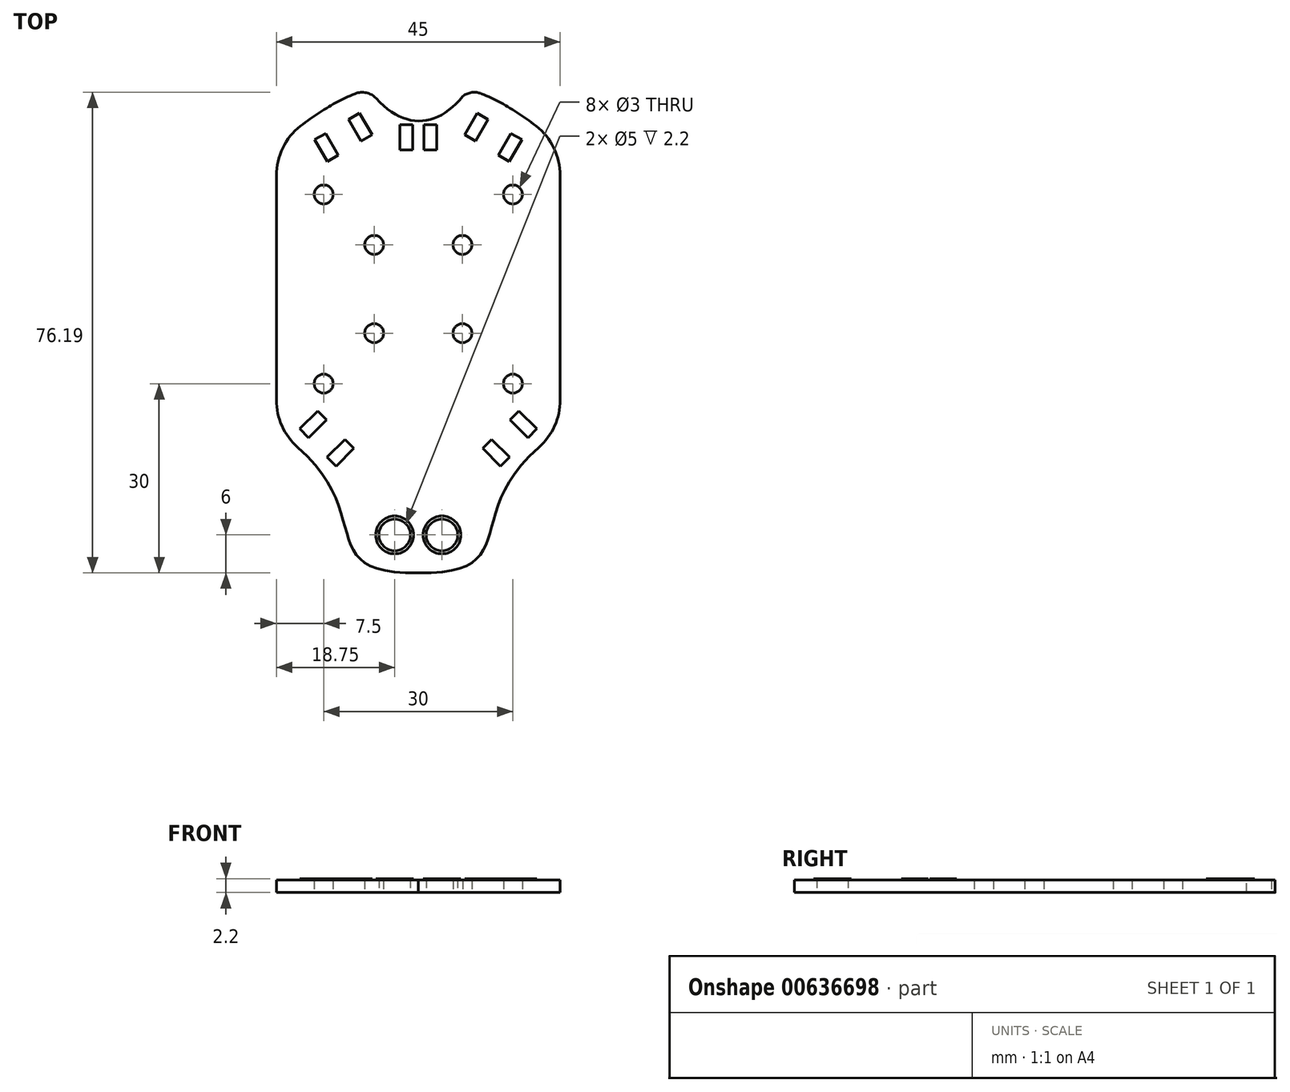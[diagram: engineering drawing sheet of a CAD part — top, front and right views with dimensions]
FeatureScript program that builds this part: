
annotation { "Feature Type Name" : "Feature", "Feature Type Description" : "" }
export const myFeature = defineFeature(function(context is Context, id is Id, definition is map)
    precondition{}
    {
        {
            var Q0;
            Q0=qCreatedBy(makeId("Top.planeOp"),FACE);
            var sketch = newSketch(context, id + "F0", { "sketchPlane" : qUnion([Q0])});
            skPoint(sketch, "E0.middle", {"position": v(0, 0) * mm});
            skCircle(sketch, "E1", {"center": v(15, 15) * mm, "radius": 1.5 * mm});
            skLineSegment(sketch, "E2.top", {"start": v(22.5, -22.5) * mm, "end": v(22.48, -22.5) * mm});
            skLineSegment(sketch, "E2.left", {"start": v(22.5, 17.98) * mm, "end": v(22.5, -17.6) * mm});
            skLineSegment(sketch, "E2.right", {"start": v(-22.5, 17.98) * mm, "end": v(-22.5, -17.6) * mm});
            skLineSegment(sketch, "E3.bottom", {"start": v(-22.5, -22.5) * mm, "end": v(-21.22, -22.5) * mm});
            skFitSpline(sketch, "E4", {"points": [v(-22.5, -22.5) * mm, v(0, -45) * mm], "startDerivative": vector(52.63, -35.78) * mm, "endDerivative": vector(54.24, 0.81) * mm});
            skArc(sketch, "E5.filletArc", {"start": v(-22.5, -17.6) * mm, "mid": v(-21.6, -21.73) * mm, "end": v(-19.1, -25.12) * mm});
            skArc(sketch, "E6.MirrorCS", {"start": v(22.5, -17.6) * mm, "mid": v(21.6, -21.73) * mm, "end": v(19.1, -25.12) * mm});
            skFitSpline(sketch, "E7.MirrorCS", {"points": [v(22.5, -22.5) * mm, v(0, -45) * mm], "startDerivative": vector(-52.63, -35.78) * mm, "endDerivative": vector(-54.24, 0.81) * mm});
            skLineSegment(sketch, "E8.trimOffspring", {"start": v(-21.22, -22.5) * mm, "end": v(-22.5, -22.5) * mm});
            skCircle(sketch, "E9", {"center": v(-3.75, -39) * mm, "radius": 2.5 * mm});
            skCircle(sketch, "E10", {"center": v(3.75, -39) * mm, "radius": 2.5 * mm});
            skCircle(sketch, "E11", {"center": v(-7, -7) * mm, "radius": 1.5 * mm});
            skCircle(sketch, "E12.MirrorC", {"center": v(7, -7) * mm, "radius": 1.5 * mm});
            skCircle(sketch, "E13.MirrorC", {"center": v(7, 7) * mm, "radius": 1.5 * mm});
            skCircle(sketch, "E14.MirrorC", {"center": v(-7, 7) * mm, "radius": 1.5 * mm});
            skFitSpline(sketch, "E15", {"points": [v(-22.5, 22.5) * mm, v(22.5, 22.5) * mm], "startDerivative": vector(43.5, 42) * mm, "endDerivative": vector(43.5, -42) * mm});
            skArc(sketch, "E16.filletArc", {"start": v(-18.67, 25.85) * mm, "mid": v(-21.5, 22.35) * mm, "end": v(-22.5, 17.98) * mm});
            skArc(sketch, "E17.filletArc", {"start": v(22.5, 17.98) * mm, "mid": v(21.5, 22.35) * mm, "end": v(18.67, 25.85) * mm});
            skEllipticalArc(sketch, "E18.trimOffspring", {});
            skLineSegment(sketch, "E19", {"start": v(-7.04, 30.9) * mm, "end": v(-7.04, 30.9) * mm});
            skFitSpline(sketch, "E20", {"points": [v(-7.87, 31.66) * mm, v(7.41, 31.02) * mm], "startDerivative": vector(14.92, -19.77) * mm, "endDerivative": vector(13.54, 17.85) * mm});
            skArc(sketch, "E21.filletArc", {"start": v(-6.68, 30.22) * mm, "mid": v(-8.23, 31.12) * mm, "end": v(-10.02, 30.97) * mm});
            skFitSpline(sketch, "E22.MirrorCS", {"points": [v(22.5, 22.5) * mm, v(-22.5, 22.5) * mm], "startDerivative": vector(-43.5, 42) * mm, "endDerivative": vector(-43.5, -42) * mm});
            skArc(sketch, "E23.MirrorCS", {"start": v(6.68, 30.22) * mm, "mid": v(8.23, 31.12) * mm, "end": v(10.02, 30.97) * mm});
            skCircle(sketch, "E24.MirrorC", {"center": v(-15, 15) * mm, "radius": 1.5 * mm});
            skCircle(sketch, "E25.MirrorC", {"center": v(-15, -15) * mm, "radius": 1.5 * mm});
            skCircle(sketch, "E26.MirrorC", {"center": v(15, -15) * mm, "radius": 1.5 * mm});
            const initialGuessF0  = {"E18.trimOffspring": [0, 0.033, 1, 0, 0.008883514441549778, 0.0030035728098805597, 5.831016555080328, 5.837561508883166]};
            skSetInitialGuess(sketch, initialGuessF0);
            skSolve(sketch);
        }
        {
            var Q0;
            Q0=makeQuery(id+"F0.imprint","IMPRINT",FACE,{"disambiguationData":[TD([[makeQuery(id+"F0.imprint","IMPRINT",EDGE,{"derivedFrom":sQuery(id+"F0.wireOp",EDGE,"E1")}),-1.0]])]});
            var Q1;
            Q1=makeQuery(id+"F0.imprint","IMPRINT",FACE,{"disambiguationData":[TD([[makeQuery(id+"F0.imprint","IMPRINT",EDGE,{"derivedFrom":sQuery(id+"F0.wireOp",EDGE,"E2.left")}),-1.0]])]});
            extrude(context, id + "F1", {"entities" : qUnion([Q0, Q1]), "depth" : 2 * mm, "offsetDistance" : 25 * mm});
        }
        {
            var Q0;
            Q0=makeQuery(id+"F1.opExtrude","CAP_FACE",FACE,{"disambiguationData":[OSD([sQuery(id+"F0.wireOp",EDGE,"E2.left"),sQuery(id+"F0.wireOp",EDGE,"E2.right"),sQuery(id+"F0.wireOp",EDGE,"E4"),sQuery(id+"F0.wireOp",EDGE,"E5.filletArc"),sQuery(id+"F0.wireOp",EDGE,"E6.MirrorCS"),sQuery(id+"F0.wireOp",EDGE,"E7.MirrorCS"),sQuery(id+"F0.wireOp",EDGE,"E9"),sQuery(id+"F0.wireOp",EDGE,"E10"),sQuery(id+"F0.wireOp",EDGE,"E12.MirrorC"),sQuery(id+"F0.wireOp",EDGE,"E11"),sQuery(id+"F0.wireOp",EDGE,"E14.MirrorC"),sQuery(id+"F0.wireOp",EDGE,"E13.MirrorC"),sQuery(id+"F0.wireOp",EDGE,"E15"),sQuery(id+"F0.wireOp",EDGE,"E16.filletArc"),sQuery(id+"F0.wireOp",EDGE,"E17.filletArc"),sQuery(id+"F0.wireOp",EDGE,"E20"),sQuery(id+"F0.wireOp",EDGE,"E21.filletArc"),sQuery(id+"F0.wireOp",EDGE,"E22.MirrorCS"),sQuery(id+"F0.wireOp",EDGE,"E23.MirrorCS"),sQuery(id+"F0.wireOp",EDGE,"E1"),sQuery(id+"F0.wireOp",EDGE,"E24.MirrorC"),sQuery(id+"F0.wireOp",EDGE,"E25.MirrorC"),sQuery(id+"F0.wireOp",EDGE,"E26.MirrorC")])],"isStart":false});
            var sketch = newSketch(context, id + "F2", { "sketchPlane" : qUnion([Q0])});
            skCircle(sketch, "E27", {"center": v(-3.75, -39) * mm, "radius": 3 * mm});
            skCircle(sketch, "E28", {"center": v(3.75, -39) * mm, "radius": 3 * mm});
            skLineSegment(sketch, "E29.bottom", {"start": v(-14.42, 20.22) * mm, "end": v(-16.42, 23.68) * mm});
            skLineSegment(sketch, "E29.top", {"start": v(-12.69, 21.22) * mm, "end": v(-14.69, 24.68) * mm});
            skLineSegment(sketch, "E29.left", {"start": v(-14.42, 20.22) * mm, "end": v(-12.69, 21.22) * mm});
            skLineSegment(sketch, "E29.right", {"start": v(-16.42, 23.68) * mm, "end": v(-14.69, 24.68) * mm});
            skLineSegment(sketch, "E30.bottom", {"start": v(-9.07, 23.44) * mm, "end": v(-11.07, 26.9) * mm});
            skLineSegment(sketch, "E30.top", {"start": v(-7.33, 24.44) * mm, "end": v(-9.33, 27.9) * mm});
            skLineSegment(sketch, "E30.left", {"start": v(-9.07, 23.44) * mm, "end": v(-7.33, 24.44) * mm});
            skLineSegment(sketch, "E30.right", {"start": v(-11.07, 26.9) * mm, "end": v(-9.33, 27.9) * mm});
            skLineSegment(sketch, "E31.MirrorCS", {"start": v(7.33, 24.44) * mm, "end": v(9.33, 27.9) * mm});
            skLineSegment(sketch, "E32.MirrorCS", {"start": v(9.07, 23.44) * mm, "end": v(7.33, 24.44) * mm});
            skLineSegment(sketch, "E33.MirrorCS", {"start": v(11.07, 26.9) * mm, "end": v(9.33, 27.9) * mm});
            skLineSegment(sketch, "E34.MirrorCS", {"start": v(14.42, 20.22) * mm, "end": v(16.42, 23.68) * mm});
            skLineSegment(sketch, "E35.MirrorCS", {"start": v(12.69, 21.22) * mm, "end": v(14.69, 24.68) * mm});
            skLineSegment(sketch, "E36.MirrorCS", {"start": v(14.42, 20.22) * mm, "end": v(12.69, 21.22) * mm});
            skLineSegment(sketch, "E37.MirrorCS", {"start": v(9.07, 23.44) * mm, "end": v(11.07, 26.9) * mm});
            skLineSegment(sketch, "E38.MirrorCS", {"start": v(16.42, 23.68) * mm, "end": v(14.69, 24.68) * mm});
            skLineSegment(sketch, "E39.bottom", {"start": v(-2.89, 22.06) * mm, "end": v(-2.89, 26.06) * mm});
            skLineSegment(sketch, "E39.top", {"start": v(-0.89, 22.06) * mm, "end": v(-0.89, 26.06) * mm});
            skLineSegment(sketch, "E39.left", {"start": v(-2.89, 22.06) * mm, "end": v(-0.89, 22.06) * mm});
            skLineSegment(sketch, "E39.right", {"start": v(-2.89, 26.06) * mm, "end": v(-0.89, 26.06) * mm});
            skLineSegment(sketch, "E40.MirrorCS", {"start": v(2.89, 22.06) * mm, "end": v(0.89, 22.06) * mm});
            skLineSegment(sketch, "E41.MirrorCS", {"start": v(0.89, 22.06) * mm, "end": v(0.89, 26.06) * mm});
            skLineSegment(sketch, "E42.MirrorCS", {"start": v(2.89, 22.06) * mm, "end": v(2.89, 26.06) * mm});
            skLineSegment(sketch, "E43.MirrorCS", {"start": v(2.89, 26.06) * mm, "end": v(0.89, 26.06) * mm});
            skLineSegment(sketch, "E44.bottom", {"start": v(13.04, -28.08) * mm, "end": v(10.21, -25.25) * mm});
            skLineSegment(sketch, "E44.top", {"start": v(14.46, -26.67) * mm, "end": v(11.63, -23.84) * mm});
            skLineSegment(sketch, "E44.left", {"start": v(13.04, -28.08) * mm, "end": v(14.46, -26.67) * mm});
            skLineSegment(sketch, "E44.right", {"start": v(10.21, -25.25) * mm, "end": v(11.63, -23.84) * mm});
            skLineSegment(sketch, "E45.bottom", {"start": v(17.38, -23.58) * mm, "end": v(14.55, -20.76) * mm});
            skLineSegment(sketch, "E45.top", {"start": v(18.8, -22.17) * mm, "end": v(15.97, -19.34) * mm});
            skLineSegment(sketch, "E45.left", {"start": v(17.38, -23.58) * mm, "end": v(18.8, -22.17) * mm});
            skLineSegment(sketch, "E45.right", {"start": v(14.55, -20.76) * mm, "end": v(15.97, -19.34) * mm});
            skLineSegment(sketch, "E46.MirrorCS", {"start": v(-14.55, -20.76) * mm, "end": v(-15.97, -19.34) * mm});
            skLineSegment(sketch, "E47.MirrorCS", {"start": v(-13.04, -28.08) * mm, "end": v(-14.46, -26.67) * mm});
            skLineSegment(sketch, "E48.MirrorCS", {"start": v(-10.21, -25.25) * mm, "end": v(-11.63, -23.84) * mm});
            skLineSegment(sketch, "E49.MirrorCS", {"start": v(-13.04, -28.08) * mm, "end": v(-10.21, -25.25) * mm});
            skLineSegment(sketch, "E50.MirrorCS", {"start": v(-17.38, -23.58) * mm, "end": v(-18.8, -22.17) * mm});
            skLineSegment(sketch, "E51.MirrorCS", {"start": v(-14.46, -26.67) * mm, "end": v(-11.63, -23.84) * mm});
            skLineSegment(sketch, "E52.MirrorCS", {"start": v(-17.38, -23.58) * mm, "end": v(-14.55, -20.76) * mm});
            skLineSegment(sketch, "E53.MirrorCS", {"start": v(-18.8, -22.17) * mm, "end": v(-15.97, -19.34) * mm});
            skSolve(sketch);
        }
        {
            var Q0;
            Q0=makeQuery(id+"F2.imprint","IMPRINT",FACE,{"disambiguationData":[TD([[makeQuery(id+"F2.imprint","IMPRINT",EDGE,{"derivedFrom":sQuery(id+"F2.wireOp",EDGE,"E29.bottom")}),-1.0]])]});
            var Q1;
            Q1=makeQuery(id+"F2.imprint","IMPRINT",FACE,{"disambiguationData":[TD([[makeQuery(id+"F2.imprint","IMPRINT",EDGE,{"derivedFrom":sQuery(id+"F2.wireOp",EDGE,"E30.bottom")}),-1.0]])]});
            var Q2;
            Q2=makeQuery(id+"F2.imprint","IMPRINT",FACE,{"disambiguationData":[TD([[makeQuery(id+"F2.imprint","IMPRINT",EDGE,{"derivedFrom":sQuery(id+"F2.wireOp",EDGE,"E39.bottom")}),-1.0]])]});
            var Q3;
            Q3=makeQuery(id+"F2.imprint","IMPRINT",FACE,{"disambiguationData":[TD([[makeQuery(id+"F2.imprint","IMPRINT",EDGE,{"derivedFrom":sQuery(id+"F2.wireOp",EDGE,"E40.MirrorCS")}),-1.0]])]});
            var Q4;
            Q4=makeQuery(id+"F2.imprint","IMPRINT",FACE,{"disambiguationData":[TD([[makeQuery(id+"F2.imprint","IMPRINT",EDGE,{"derivedFrom":sQuery(id+"F2.wireOp",EDGE,"E31.MirrorCS")}),-1.0]])]});
            var Q5;
            Q5=makeQuery(id+"F2.imprint","IMPRINT",FACE,{"disambiguationData":[TD([[makeQuery(id+"F2.imprint","IMPRINT",EDGE,{"derivedFrom":sQuery(id+"F2.wireOp",EDGE,"E34.MirrorCS")}),1.0]])]});
            var Q6;
            Q6=makeQuery(id+"F2.imprint","IMPRINT",FACE,{"disambiguationData":[TD([[makeQuery(id+"F2.imprint","IMPRINT",EDGE,{"derivedFrom":sQuery(id+"F2.wireOp",EDGE,"E46.MirrorCS")}),1.0]])]});
            var Q7;
            Q7=makeQuery(id+"F2.imprint","IMPRINT",FACE,{"disambiguationData":[TD([[makeQuery(id+"F2.imprint","IMPRINT",EDGE,{"derivedFrom":sQuery(id+"F2.wireOp",EDGE,"E47.MirrorCS")}),-1.0]])]});
            var Q8;
            Q8=makeQuery(id+"F2.imprint","IMPRINT",FACE,{"disambiguationData":[TD([[makeQuery(id+"F2.imprint","IMPRINT",EDGE,{"derivedFrom":sQuery(id+"F2.wireOp",EDGE,"E44.bottom")}),-1.0]])]});
            var Q9;
            Q9=makeQuery(id+"F2.imprint","IMPRINT",FACE,{"disambiguationData":[TD([[makeQuery(id+"F2.imprint","IMPRINT",EDGE,{"derivedFrom":sQuery(id+"F2.wireOp",EDGE,"E45.bottom")}),-1.0]])]});
            var Q10;
            Q10=makeQuery(id+"F2.imprint","IMPRINT",FACE,{"disambiguationData":[TD([[makeQuery(id+"F2.imprint","IMPRINT",EDGE,{"derivedFrom":sQuery(id+"F2.wireOp",EDGE,"E27")}),1.0]])]});
            var Q11;
            Q11=makeQuery(id+"F2.imprint","IMPRINT",FACE,{"disambiguationData":[TD([[makeQuery(id+"F2.imprint","IMPRINT",EDGE,{"derivedFrom":sQuery(id+"F2.wireOp",EDGE,"E28")}),1.0]])]});
            extrude(context, id + "F3", {"entities" : qUnion([Q0, Q1, Q2, Q3, Q4, Q5, Q6, Q7, Q8, Q9, Q10, Q11]), "operationType" : NewBodyOperationType.ADD, "depth" : 0.2 * mm, "offsetDistance" : 25 * mm});
        }
    });
